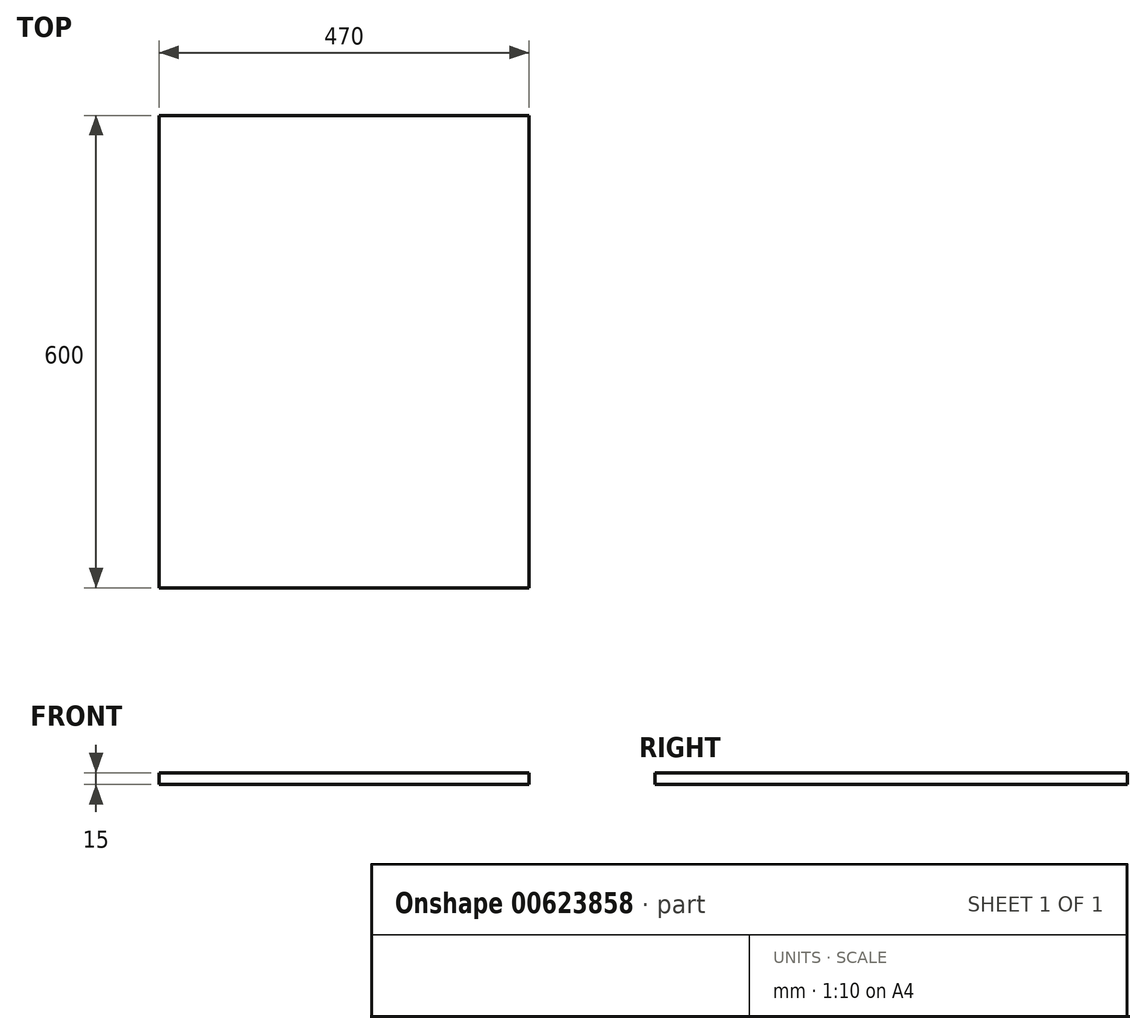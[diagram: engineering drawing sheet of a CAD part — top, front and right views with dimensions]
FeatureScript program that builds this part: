
annotation { "Feature Type Name" : "Feature", "Feature Type Description" : "" }
export const myFeature = defineFeature(function(context is Context, id is Id, definition is map)
    precondition{}
    {
        {
            var Q0;
            Q0=qCreatedBy(makeId("Top.planeOp"),FACE);
            var sketch = newSketch(context, id + "F0", { "sketchPlane" : qUnion([Q0])});
            skLineSegment(sketch, "E0.bottom", {"start": v(0, 0) * mm, "end": v(470, 0) * mm});
            skLineSegment(sketch, "E0.top", {"start": v(0, 600) * mm, "end": v(470, 600) * mm});
            skLineSegment(sketch, "E0.left", {"start": v(0, 0) * mm, "end": v(0, 600) * mm});
            skLineSegment(sketch, "E0.right", {"start": v(470, 0) * mm, "end": v(470, 600) * mm});
            skSolve(sketch);
        }
        {
            var Q0;
            Q0 = qSketchRegion(id + "F0", true);
            extrude(context, id + "F1", {"entities" : qUnion([Q0]), "depth" : 15 * mm, "offsetDistance" : 25 * mm});
        }
    });
